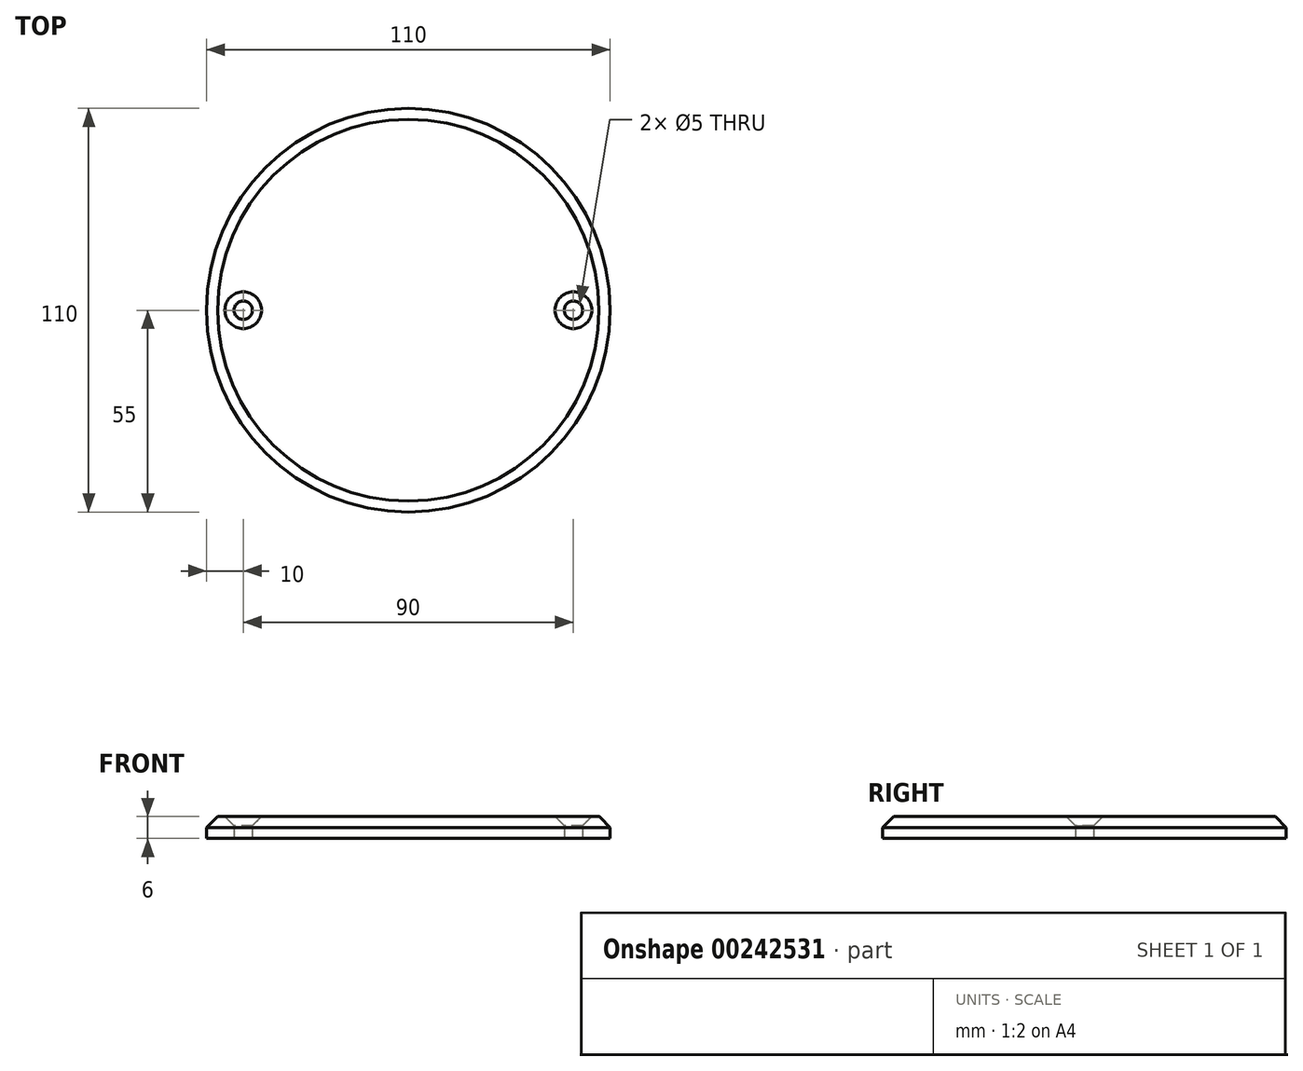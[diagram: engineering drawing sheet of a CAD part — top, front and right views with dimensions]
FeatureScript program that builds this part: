
annotation { "Feature Type Name" : "Feature", "Feature Type Description" : "" }
export const myFeature = defineFeature(function(context is Context, id is Id, definition is map)
    precondition{}
    {
        {
            var Q0;
            Q0=qCreatedBy(makeId("Top.planeOp"),FACE);
            var sketch = newSketch(context, id + "F0", { "sketchPlane" : qUnion([Q0])});
            skLineSegment(sketch, "E0", {"start": v(-45, 0) * mm, "end": v(45, 0) * mm, "construction": true});
            skCircle(sketch, "E1", {"center": v(-45, 0) * mm, "radius": 2.5 * mm});
            skCircle(sketch, "E2", {"center": v(45, 0) * mm, "radius": 2.5 * mm});
            skCircle(sketch, "E3", {"center": v(0, 0) * mm, "radius": 55 * mm});
            skSolve(sketch);
        }
        {
            var Q0;
            Q0=makeQuery(id+"F0.imprint","IMPRINT",FACE,{"disambiguationData":[TD([[makeQuery(id+"F0.imprint","IMPRINT",EDGE,{"derivedFrom":sQuery(id+"F0.wireOp",EDGE,"E1")}),-1.0]])]});
            extrude(context, id + "F1", {"entities" : qUnion([Q0]), "depth" : 6 * mm});
        }
        {
            var Q0;
            Q0=makeQuery(id+"F1.opExtrude","CAP_EDGE",EDGE,{"disambiguationData":[OSD([sQuery(id+"F0.wireOp",EDGE,"E3")])],"isStart":false});
            chamfer(context, id + "F2", {"entities" : qUnion([Q0]), "width" : 3 * mm, "tangentPropagation" : true});
        }
        {
            var Q0;
            Q0=makeQuery(id+"F1.opExtrude","CAP_EDGE",EDGE,{"disambiguationData":[OSD([sQuery(id+"F0.wireOp",EDGE,"E1")])],"isStart":false});
            var Q1;
            Q1=makeQuery(id+"F1.opExtrude","CAP_EDGE",EDGE,{"disambiguationData":[OSD([sQuery(id+"F0.wireOp",EDGE,"E2")])],"isStart":false});
            chamfer(context, id + "F3", {"entities" : qUnion([Q0, Q1]), "width" : 2.5 * mm, "tangentPropagation" : true});
        }
    });
